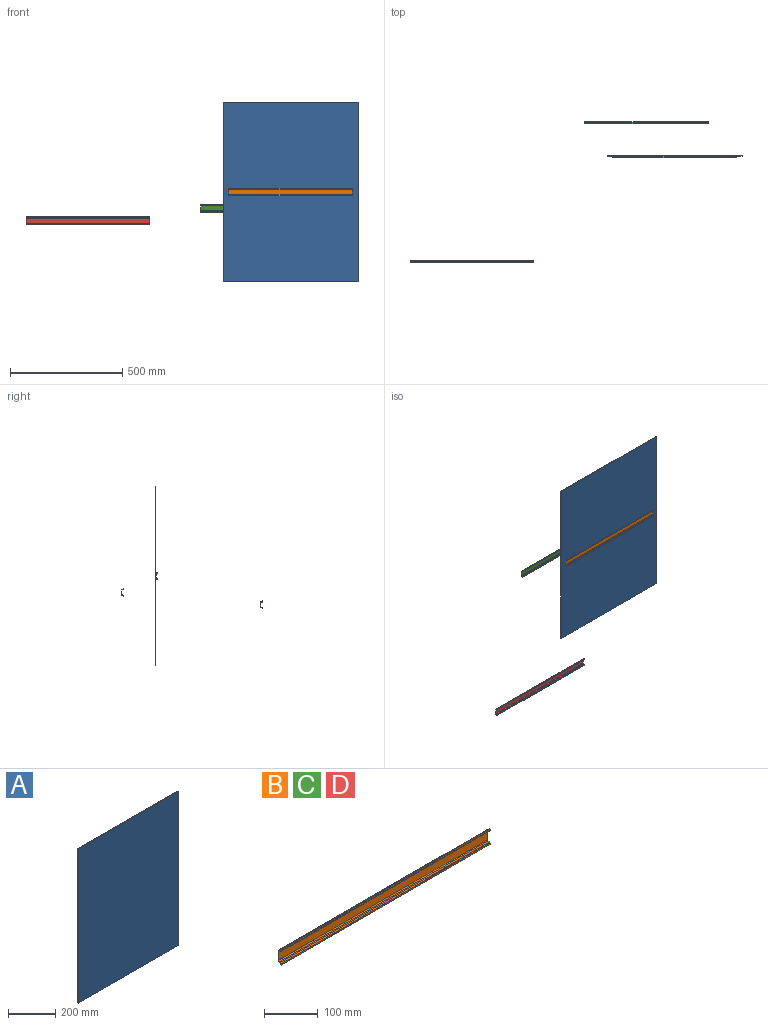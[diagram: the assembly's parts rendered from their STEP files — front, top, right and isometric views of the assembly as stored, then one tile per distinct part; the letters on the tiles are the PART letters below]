
ASSEMBLY  parts=4 mates=3
PART A: 6 faces, bbox 600x2x800 mm
  f0: plane 600x2mm, normal (0,0,1), area 1200mm2, adj f1,f3,f4,f5
  f1: plane 800x2mm, normal (-1,0,0), area 1600mm2, adj f0,f2,f4,f5
  f2: plane 600x2mm, normal (0,0,-1), area 1200mm2, adj f1,f3,f4,f5
  f3: plane 800x2mm, normal (1,0,0), area 1600mm2, adj f0,f2,f4,f5
  f4: plane 800x600mm, normal (0,-1,0), area 480000mm2, adj f0,f1,f2,f3
  f5: plane 800x600mm, normal (0,1,0), area 480000mm2, adj f0,f1,f2,f3
PART B: 22 faces, bbox 550x8.5x35 mm
  f0: plane 550x21mm, normal (0,1,0), area 11550mm2, adj f1,f19,f20,f21
  f1: cylinder r=3mm len=550mm, axis (-1,0,0), area 2591.8mm2, adj f0,f2,f20,f21
  f2: plane 550x3.5mm, normal (0,0,1), area 1925mm2, adj f1,f3,f20,f21
  f3: cylinder r=1mm len=550mm, axis (-1,0,0), area 863.9mm2, adj f2,f4,f20,f21
  f4: plane 550x3mm, normal (0,1,0), area 1650mm2, adj f3,f5,f20,f21
  f5: plane 550x1mm, normal (0,0,1), area 550mm2, adj f4,f6,f20,f21
  f6: plane 550x3mm, normal (0,-1,0), area 1650mm2, adj f5,f7,f20,f21
  f7: cylinder r=2mm len=550mm, axis (-1,0,0), area 1727.9mm2, adj f6,f8,f20,f21
  f8: plane 550x3.5mm, normal (0,0,-1), area 1925mm2, adj f7,f9,f20,f21
  f9: cylinder r=2mm len=550mm, axis (-1,0,0), area 1727.9mm2, adj f8,f10,f20,f21
  f10: plane 550x21mm, normal (0,-1,0), area 11550mm2, adj f9,f11,f20,f21
  f11: cylinder r=2mm len=550mm, axis (-1,0,0), area 1727.9mm2, adj f10,f12,f20,f21
  f12: plane 550x3.5mm, normal (0,0,1), area 1925mm2, adj f11,f13,f20,f21
  f13: cylinder r=2mm len=550mm, axis (-1,0,0), area 1727.9mm2, adj f12,f14,f20,f21
  f14: plane 550x3mm, normal (0,-1,0), area 1650mm2, adj f13,f15,f20,f21
  f15: plane 550x1mm, normal (0,0,-1), area 550mm2, adj f14,f16,f20,f21
  f16: plane 550x3mm, normal (0,1,0), area 1650mm2, adj f15,f17,f20,f21
  f17: cylinder r=1mm len=550mm, axis (-1,0,0), area 863.9mm2, adj f16,f18,f20,f21
  f18: plane 550x3.5mm, normal (0,0,-1), area 1925mm2, adj f17,f19,f20,f21
  f19: cylinder r=3mm len=550mm, axis (-1,0,0), area 2591.8mm2, adj f0,f18,f20,f21
  f20: plane 35x8.5mm, normal (1,0,0), area 46.6mm2, adj f0,f1,f2,f3,f4,f5,f6,f7
  f21: plane 35x8.5mm, normal (-1,0,0), area 46.6mm2, adj f0,f1,f2,f3,f4,f5,f6,f7
PART C: same geometry as B
PART D: same geometry as B
PLACE A t=(252.43,3,13.77)mm
PLACE B at identity
PLACE C t=(-124.49,152.51,-72.59)mm
PLACE D t=(-901.84,-464.31,-128.54)mm
MATE parallel C.f0 <-> A.f4  axis (0,1,0) through (150.51,153.51,-60.09)mm
MATE parallel A.f4 <-> B.f0  axis (0,-1,0) through (275,1,12.5)mm
MATE parallel A.f4 <-> D.f0  axis (0,-1,0) through (275,1,12.5)mm
